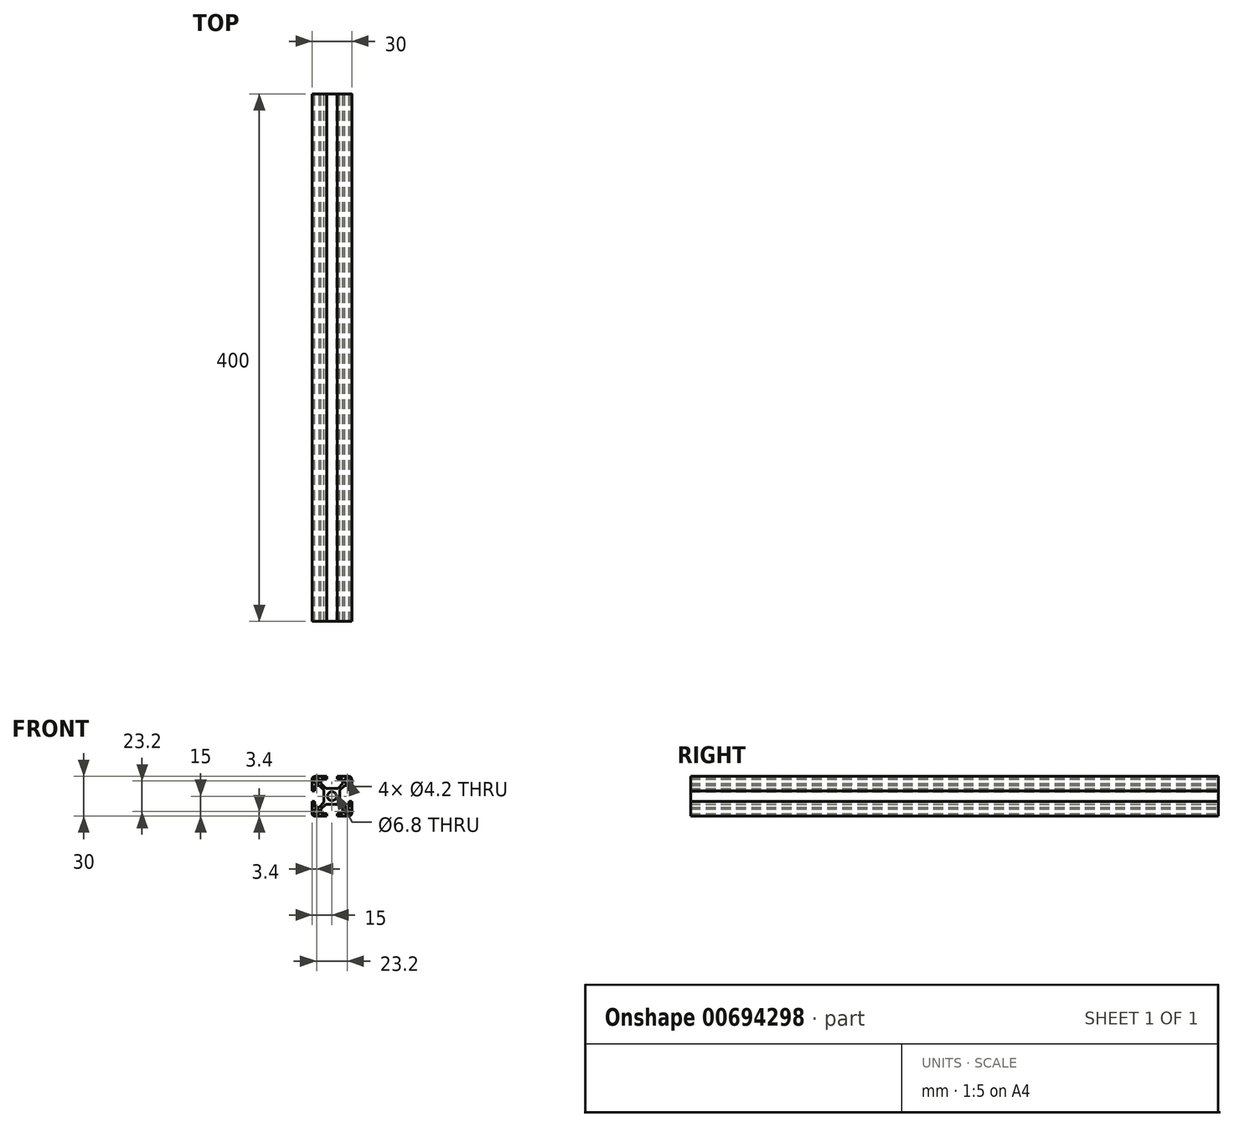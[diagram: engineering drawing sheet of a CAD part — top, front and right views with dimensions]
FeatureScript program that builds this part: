
annotation { "Feature Type Name" : "Feature", "Feature Type Description" : "" }
export const myFeature = defineFeature(function(context is Context, id is Id, definition is map)
    precondition{}
    {
        {
            var Q0;
            Q0=qCreatedBy(makeId("Front.planeOp"),FACE);
            var sketch = newSketch(context, id + "F0", { "sketchPlane" : qUnion([Q0])});
            skLineSegment(sketch, "E0", {"start": v(0, 6) * mm, "end": v(-4.59, 6) * mm});
            skLineSegment(sketch, "E1", {"start": v(-4.59, 6) * mm, "end": v(-8.25, 9.66) * mm});
            skLineSegment(sketch, "E2", {"start": v(-8.25, 9.66) * mm, "end": v(-8.25, 13) * mm});
            skLineSegment(sketch, "E3", {"start": v(-8.25, 13) * mm, "end": v(-4, 13) * mm});
            skLineSegment(sketch, "E4", {"start": v(-4, 13) * mm, "end": v(-4, 15) * mm});
            skLineSegment(sketch, "E5", {"start": v(-4, 15) * mm, "end": v(-13, 15) * mm});
            skLineSegment(sketch, "E6", {"start": v(-15, 13) * mm, "end": v(-15, 4) * mm});
            skLineSegment(sketch, "E7", {"start": v(-15, 4) * mm, "end": v(-13, 4) * mm});
            skLineSegment(sketch, "E8", {"start": v(-13, 4) * mm, "end": v(-13, 8.25) * mm});
            skLineSegment(sketch, "E9", {"start": v(-13, 8.25) * mm, "end": v(-9.66, 8.25) * mm});
            skLineSegment(sketch, "E10", {"start": v(-9.66, 8.25) * mm, "end": v(-6, 4.59) * mm});
            skLineSegment(sketch, "E11", {"start": v(-6, 4.59) * mm, "end": v(-6, 0) * mm});
            skLineSegment(sketch, "E12", {"start": v(-6, 0) * mm, "end": v(0, 0) * mm, "construction": true});
            skLineSegment(sketch, "E13", {"start": v(0, 0) * mm, "end": v(0, 6) * mm, "construction": true});
            skArc(sketch, "E14", {"start": v(0, 3.4) * mm, "mid": v(-2.4, 2.4) * mm, "end": v(-3.4, 0) * mm});
            skCircle(sketch, "E15", {"center": v(-11.6, 11.6) * mm, "radius": 2.1 * mm});
            skLineSegment(sketch, "E16", {"start": v(0, 0) * mm, "end": v(-7.38, 7.38) * mm, "construction": true});
            skLineSegment(sketch, "E17.1.0", {"start": v(-8.25, -13) * mm, "end": v(-8.25, -9.66) * mm});
            skLineSegment(sketch, "E17.1.1", {"start": v(-4, -15) * mm, "end": v(-4, -13) * mm});
            skLineSegment(sketch, "E17.1.2", {"start": v(-4, -13) * mm, "end": v(-8.25, -13) * mm});
            skLineSegment(sketch, "E17.1.3", {"start": v(-15, -4) * mm, "end": v(-15, -13) * mm});
            skLineSegment(sketch, "E17.1.4", {"start": v(-8.25, -9.66) * mm, "end": v(-4.59, -6) * mm});
            skLineSegment(sketch, "E17.1.5", {"start": v(-13, -15) * mm, "end": v(-4, -15) * mm});
            skLineSegment(sketch, "E17.1.6", {"start": v(-4.59, -6) * mm, "end": v(0, -6) * mm});
            skLineSegment(sketch, "E17.1.7", {"start": v(0, -6) * mm, "end": v(0, 0) * mm, "construction": true});
            skLineSegment(sketch, "E17.1.8", {"start": v(0, 0) * mm, "end": v(-6, 0) * mm, "construction": true});
            skLineSegment(sketch, "E17.1.9", {"start": v(-13, -4) * mm, "end": v(-15, -4) * mm});
            skLineSegment(sketch, "E17.1.10", {"start": v(-13, -8.25) * mm, "end": v(-13, -4) * mm});
            skArc(sketch, "E17.1.11", {"start": v(-3.4, 0) * mm, "mid": v(-2.4, -2.4) * mm, "end": v(0, -3.4) * mm});
            skLineSegment(sketch, "E17.1.12", {"start": v(-9.66, -8.25) * mm, "end": v(-13, -8.25) * mm});
            skLineSegment(sketch, "E17.1.13", {"start": v(0, 0) * mm, "end": v(-7.38, -7.38) * mm, "construction": true});
            skLineSegment(sketch, "E17.1.14", {"start": v(-6, -4.59) * mm, "end": v(-9.66, -8.25) * mm});
            skCircle(sketch, "E17.1.15", {"center": v(-11.6, -11.6) * mm, "radius": 2.1 * mm});
            skLineSegment(sketch, "E17.1.16", {"start": v(-6, 0) * mm, "end": v(-6, -4.59) * mm});
            skLineSegment(sketch, "E17.2.0", {"start": v(13, -8.25) * mm, "end": v(9.66, -8.25) * mm});
            skLineSegment(sketch, "E17.2.1", {"start": v(15, -4) * mm, "end": v(13, -4) * mm});
            skLineSegment(sketch, "E17.2.2", {"start": v(13, -4) * mm, "end": v(13, -8.25) * mm});
            skLineSegment(sketch, "E17.2.3", {"start": v(4, -15) * mm, "end": v(13, -15) * mm});
            skLineSegment(sketch, "E17.2.4", {"start": v(9.66, -8.25) * mm, "end": v(6, -4.59) * mm});
            skLineSegment(sketch, "E17.2.5", {"start": v(15, -13) * mm, "end": v(15, -4) * mm});
            skLineSegment(sketch, "E17.2.6", {"start": v(6, -4.59) * mm, "end": v(6, 0) * mm});
            skLineSegment(sketch, "E17.2.7", {"start": v(6, 0) * mm, "end": v(0, 0) * mm, "construction": true});
            skLineSegment(sketch, "E17.2.8", {"start": v(0, 0) * mm, "end": v(0, -6) * mm, "construction": true});
            skLineSegment(sketch, "E17.2.9", {"start": v(4, -13) * mm, "end": v(4, -15) * mm});
            skLineSegment(sketch, "E17.2.10", {"start": v(8.25, -13) * mm, "end": v(4, -13) * mm});
            skArc(sketch, "E17.2.11", {"start": v(0, -3.4) * mm, "mid": v(2.4, -2.4) * mm, "end": v(3.4, 0) * mm});
            skLineSegment(sketch, "E17.2.12", {"start": v(8.25, -9.66) * mm, "end": v(8.25, -13) * mm});
            skLineSegment(sketch, "E17.2.13", {"start": v(0, 0) * mm, "end": v(7.38, -7.38) * mm, "construction": true});
            skLineSegment(sketch, "E17.2.14", {"start": v(4.59, -6) * mm, "end": v(8.25, -9.66) * mm});
            skCircle(sketch, "E17.2.15", {"center": v(11.6, -11.6) * mm, "radius": 2.1 * mm});
            skLineSegment(sketch, "E17.2.16", {"start": v(0, -6) * mm, "end": v(4.59, -6) * mm});
            skLineSegment(sketch, "E17.3.0", {"start": v(8.25, 13) * mm, "end": v(8.25, 9.66) * mm});
            skLineSegment(sketch, "E17.3.1", {"start": v(4, 15) * mm, "end": v(4, 13) * mm});
            skLineSegment(sketch, "E17.3.2", {"start": v(4, 13) * mm, "end": v(8.25, 13) * mm});
            skLineSegment(sketch, "E17.3.3", {"start": v(15, 4) * mm, "end": v(15, 13) * mm});
            skLineSegment(sketch, "E17.3.4", {"start": v(8.25, 9.66) * mm, "end": v(4.59, 6) * mm});
            skLineSegment(sketch, "E17.3.5", {"start": v(13, 15) * mm, "end": v(4, 15) * mm});
            skLineSegment(sketch, "E17.3.6", {"start": v(4.59, 6) * mm, "end": v(0, 6) * mm});
            skLineSegment(sketch, "E17.3.7", {"start": v(0, 6) * mm, "end": v(0, 0) * mm, "construction": true});
            skLineSegment(sketch, "E17.3.8", {"start": v(0, 0) * mm, "end": v(6, 0) * mm, "construction": true});
            skLineSegment(sketch, "E17.3.9", {"start": v(13, 4) * mm, "end": v(15, 4) * mm});
            skLineSegment(sketch, "E17.3.10", {"start": v(13, 8.25) * mm, "end": v(13, 4) * mm});
            skArc(sketch, "E17.3.11", {"start": v(3.4, 0) * mm, "mid": v(2.4, 2.4) * mm, "end": v(0, 3.4) * mm});
            skLineSegment(sketch, "E17.3.12", {"start": v(9.66, 8.25) * mm, "end": v(13, 8.25) * mm});
            skLineSegment(sketch, "E17.3.13", {"start": v(0, 0) * mm, "end": v(7.38, 7.38) * mm, "construction": true});
            skLineSegment(sketch, "E17.3.14", {"start": v(6, 4.59) * mm, "end": v(9.66, 8.25) * mm});
            skCircle(sketch, "E17.3.15", {"center": v(11.6, 11.6) * mm, "radius": 2.1 * mm});
            skLineSegment(sketch, "E17.3.16", {"start": v(6, 0) * mm, "end": v(6, 4.59) * mm});
            skPoint(sketch, "E18.visualSharp", {"position": v(-15, 15) * mm});
            skArc(sketch, "E18.filletArc", {"start": v(-13, 15) * mm, "mid": v(-14.41, 14.41) * mm, "end": v(-15, 13) * mm});
            skPoint(sketch, "E19.visualSharp", {"position": v(15, 15) * mm});
            skArc(sketch, "E19.filletArc", {"start": v(15, 13) * mm, "mid": v(14.41, 14.41) * mm, "end": v(13, 15) * mm});
            skPoint(sketch, "E20.visualSharp", {"position": v(15, -15) * mm});
            skArc(sketch, "E20.filletArc", {"start": v(13, -15) * mm, "mid": v(14.41, -14.41) * mm, "end": v(15, -13) * mm});
            skPoint(sketch, "E21.visualSharp", {"position": v(-15, -15) * mm});
            skArc(sketch, "E21.filletArc", {"start": v(-15, -13) * mm, "mid": v(-14.41, -14.41) * mm, "end": v(-13, -15) * mm});
            skSolve(sketch);
        }
        {
            var Q0;
            Q0=qSketchRegion(id+"F0",true);
            extrude(context, id + "F1", {"entities" : qUnion([Q0]), "depth" : 400 * mm, "offsetDistance" : 25 * mm});
        }
    });
